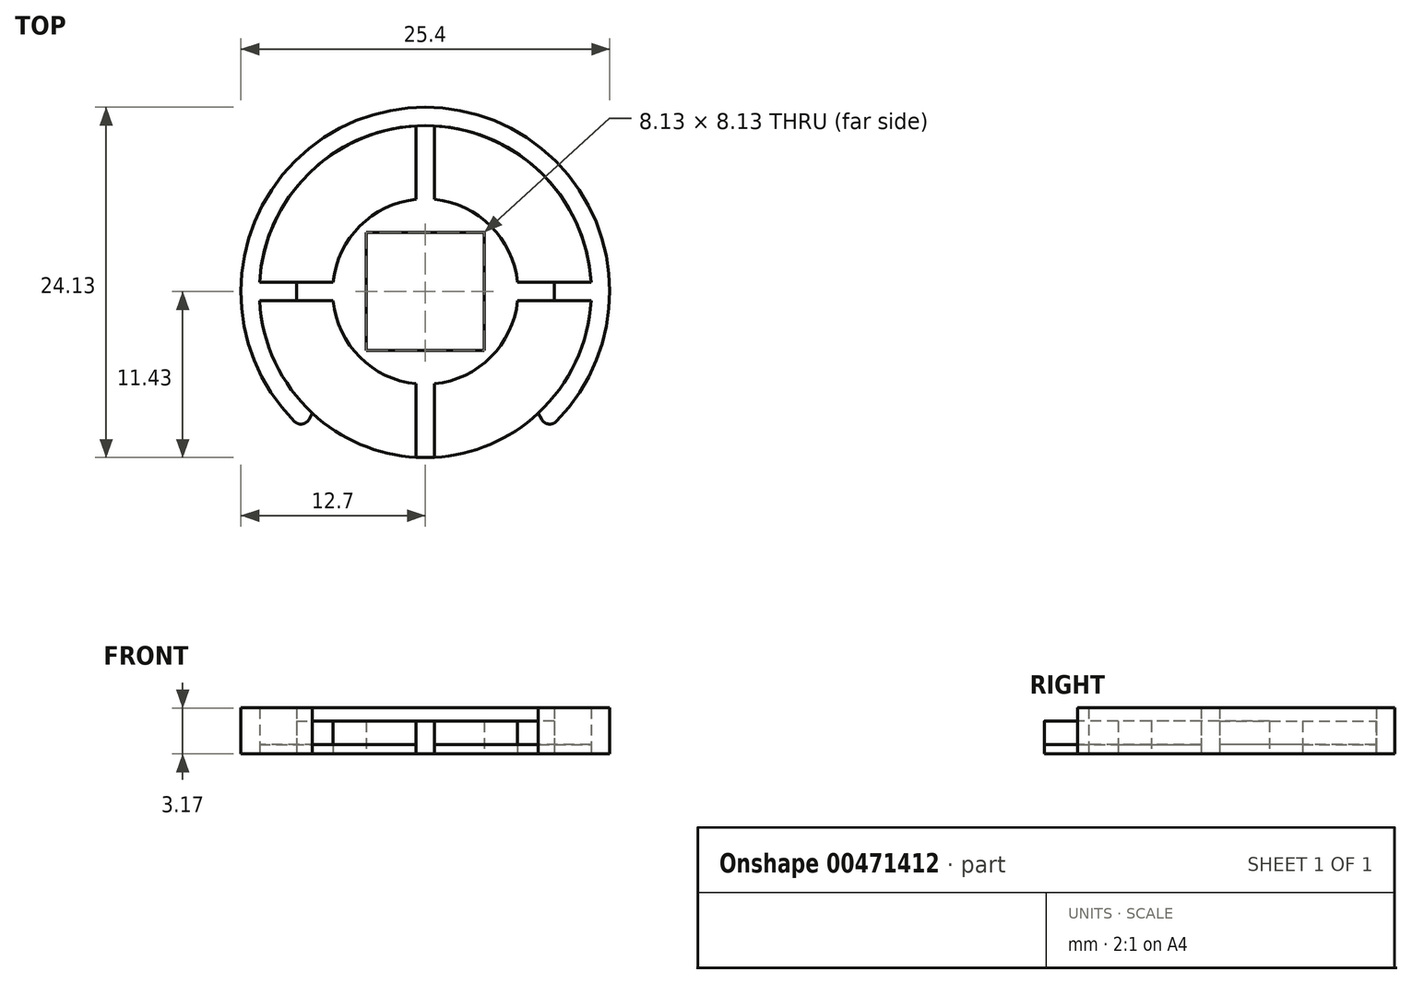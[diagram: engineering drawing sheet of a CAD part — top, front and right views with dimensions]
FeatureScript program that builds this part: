
annotation { "Feature Type Name" : "Feature", "Feature Type Description" : "" }
export const myFeature = defineFeature(function(context is Context, id is Id, definition is map)
    precondition{}
    {
        {
            var Q0;
            Q0=qCreatedBy(makeId("Top.planeOp"),FACE);
            var sketch = newSketch(context, id + "F0", { "sketchPlane" : qUnion([Q0])});
            skCircle(sketch, "E0", {"center": v(0, 0) * mm, "radius": 12.7 * mm});
            skLineSegment(sketch, "E1.bottom", {"start": v(-4.06, 4.06) * mm, "end": v(4.06, 4.06) * mm});
            skLineSegment(sketch, "E1.top", {"start": v(-4.06, -4.06) * mm, "end": v(4.06, -4.06) * mm});
            skLineSegment(sketch, "E1.left", {"start": v(-4.06, 4.06) * mm, "end": v(-4.06, -4.06) * mm});
            skLineSegment(sketch, "E1.right", {"start": v(4.06, 4.06) * mm, "end": v(4.06, -4.06) * mm});
            skCircle(sketch, "E2", {"center": v(0, 0) * mm, "radius": 5.75 * mm, "construction": true});
            skCircle(sketch, "E3", {"center": v(0, 0) * mm, "radius": 6.38 * mm});
            skCircle(sketch, "E4", {"center": v(0, 0) * mm, "radius": 11.43 * mm});
            skLineSegment(sketch, "E5", {"start": v(-44.52, 0) * mm, "end": v(37.34, 0) * mm, "construction": true});
            skLineSegment(sketch, "E6", {"start": v(-0.64, 6.35) * mm, "end": v(-0.64, 11.41) * mm});
            skLineSegment(sketch, "E7.MirrorCS", {"start": v(0.64, 6.35) * mm, "end": v(0.63, 11.41) * mm});
            skLineSegment(sketch, "E8.MirrorCS", {"start": v(-0.64, -6.35) * mm, "end": v(-0.64, -11.41) * mm});
            skLineSegment(sketch, "E9.MirrorCS", {"start": v(0.64, -6.35) * mm, "end": v(0.63, -11.41) * mm});
            skLineSegment(sketch, "E10", {"start": v(-11.41, 0.64) * mm, "end": v(-6.35, 0.64) * mm});
            skLineSegment(sketch, "E11.MirrorCS", {"start": v(-11.41, -0.64) * mm, "end": v(-6.35, -0.64) * mm});
            skLineSegment(sketch, "E12", {"start": v(0, -16.37) * mm, "end": v(0, 17.47) * mm, "construction": true});
            skLineSegment(sketch, "E13.MirrorCS", {"start": v(11.41, 0.64) * mm, "end": v(6.35, 0.64) * mm});
            skLineSegment(sketch, "E14.MirrorCS", {"start": v(11.41, -0.64) * mm, "end": v(6.35, -0.64) * mm});
            skLineSegment(sketch, "E15", {"start": v(-8.87, 0.64) * mm, "end": v(-8.87, -0.64) * mm});
            skLineSegment(sketch, "E16.MirrorCS", {"start": v(8.87, 0.64) * mm, "end": v(8.87, -0.64) * mm});
            skLineSegment(sketch, "E17", {"start": v(0, 0) * mm, "end": v(-14.65, -25.37) * mm, "construction": true});
            skLineSegment(sketch, "E18.MirrorCS", {"start": v(0, 0) * mm, "end": v(14.65, -25.37) * mm, "construction": true});
            skLineSegment(sketch, "E19", {"start": v(-8.42, -9.5) * mm, "end": v(-7.77, -8.38) * mm});
            skLineSegment(sketch, "E20.MirrorCS", {"start": v(8.42, -9.5) * mm, "end": v(7.77, -8.38) * mm});
            skSolve(sketch);
        }
        {
            var Q0;
            Q0=makeQuery(id+"F0.imprint","IMPRINT",FACE,{"disambiguationData":[TD([[makeQuery(id+"F0.imprint","IMPRINT",EDGE,{"derivedFrom":sQuery(id+"F0.wireOp",EDGE,"E1.bottom")}),1.0]])]});
            var Q1;
            {var subQ0=sQuery(id+"F0.wireOp",EDGE,"E8.MirrorCS");Q1=makeQuery(id+"F0.imprint","IMPRINT",FACE,{"disambiguationData":[TD([[makeQuery(id+"F0.imprint","IMPRINT",EDGE,{"derivedFrom":subQ0}),1.0]])]});}
            var Q2;
            {var subQ0=sQuery(id+"F0.wireOp",EDGE,"E6");Q2=makeQuery(id+"F0.imprint","IMPRINT",FACE,{"disambiguationData":[TD([[makeQuery(id+"F0.imprint","IMPRINT",EDGE,{"derivedFrom":subQ0}),-1.0]])]});}
            var Q3;
            {var subQ5=sQuery(id+"F0.wireOp",EDGE,"E15");Q3=makeQuery(id+"F0.imprint","IMPRINT",FACE,{"disambiguationData":[TD([[makeQuery(id+"F0.imprint","IMPRINT",EDGE,{"derivedFrom":subQ5}),1.0]])]});}
            var Q4;
            {var subQ5=sQuery(id+"F0.wireOp",EDGE,"E16.MirrorCS");Q4=makeQuery(id+"F0.imprint","IMPRINT",FACE,{"disambiguationData":[TD([[makeQuery(id+"F0.imprint","IMPRINT",EDGE,{"derivedFrom":subQ5}),-1.0]])]});}
            extrude(context, id + "F1", {"entities" : qUnion([Q0, Q1, Q2, Q3, Q4]), "depth" : 2.26 * mm});
        }
        {
            var Q0;
            {var subQ0=sQuery(id+"F0.wireOp",EDGE,"E6");Q0=makeQuery(id+"F0.imprint","IMPRINT",FACE,{"disambiguationData":[TD([[makeQuery(id+"F0.imprint","IMPRINT",EDGE,{"derivedFrom":subQ0}),1.0]])]});}
            var Q1;
            {var subQ4=sQuery(id+"F0.wireOp",EDGE,"E7.MirrorCS");Q1=makeQuery(id+"F0.imprint","IMPRINT",FACE,{"disambiguationData":[TD([[makeQuery(id+"F0.imprint","IMPRINT",EDGE,{"derivedFrom":subQ4}),-1.0]])]});}
            var Q2;
            {var subQ0=sQuery(id+"F0.wireOp",EDGE,"E9.MirrorCS");Q2=makeQuery(id+"F0.imprint","IMPRINT",FACE,{"disambiguationData":[TD([[makeQuery(id+"F0.imprint","IMPRINT",EDGE,{"derivedFrom":subQ0}),1.0]])]});}
            var Q3;
            {var subQ0=sQuery(id+"F0.wireOp",EDGE,"E8.MirrorCS");Q3=makeQuery(id+"F0.imprint","IMPRINT",FACE,{"disambiguationData":[TD([[makeQuery(id+"F0.imprint","IMPRINT",EDGE,{"derivedFrom":subQ0}),-1.0]])]});}
            extrude(context, id + "F2", {"entities" : qUnion([Q0, Q1, Q2, Q3]), "depth" : 0.64 * mm});
        }
        {
            var Q0;
            {var subQ5=sQuery(id+"F0.wireOp",EDGE,"E15");Q0=makeQuery(id+"F0.imprint","IMPRINT",FACE,{"disambiguationData":[TD([[makeQuery(id+"F0.imprint","IMPRINT",EDGE,{"derivedFrom":subQ5}),-1.0]])]});}
            var Q1;
            {var subQ5=sQuery(id+"F0.wireOp",EDGE,"E16.MirrorCS");Q1=makeQuery(id+"F0.imprint","IMPRINT",FACE,{"disambiguationData":[TD([[makeQuery(id+"F0.imprint","IMPRINT",EDGE,{"derivedFrom":subQ5}),1.0]])]});}
            var Q2;
            {var subQ5=sQuery(id+"F0.wireOp",EDGE,"E19");Q2=makeQuery(id+"F0.imprint","IMPRINT",FACE,{"disambiguationData":[TD([[makeQuery(id+"F0.imprint","IMPRINT",EDGE,{"derivedFrom":subQ5}),1.0]])]});}
            extrude(context, id + "F3", {"entities" : qUnion([Q0, Q1, Q2]), "depth" : 3.17 * mm});
        }
        {
            var Q0;
            Q0=makeQuery(id+"F3.opExtrude","SWEPT_EDGE",EDGE,{"disambiguationData":[OSD([sQuery(id+"F0.wireOp",EDGE,"E0"),sQuery(id+"F0.wireOp",EDGE,"E19")])]});
            var Q1;
            Q1=makeQuery(id+"F3.opExtrude","SWEPT_EDGE",EDGE,{"disambiguationData":[OSD([sQuery(id+"F0.wireOp",EDGE,"E0"),sQuery(id+"F0.wireOp",EDGE,"E20.MirrorCS")])]});
            fillet(context, id + "F4", {"entities" : qUnion([Q0, Q1]), "radius" : 0.64 * mm, "tangentPropagation" : true, "allowEdgeOverflow" : false});
        }
    });
